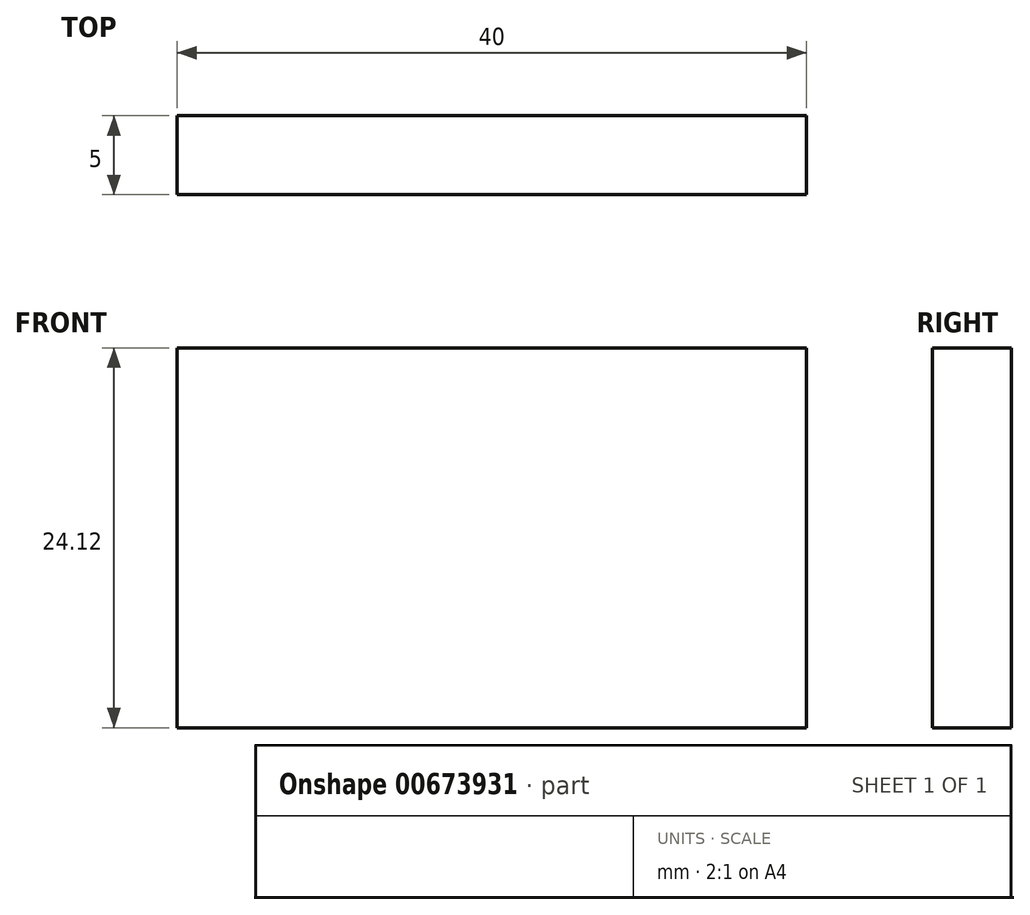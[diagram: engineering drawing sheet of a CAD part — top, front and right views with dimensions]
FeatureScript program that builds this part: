
annotation { "Feature Type Name" : "Feature", "Feature Type Description" : "" }
export const myFeature = defineFeature(function(context is Context, id is Id, definition is map)
    precondition{}
    {
        {
            var Q0;
            Q0=qCreatedBy(makeId("Front.planeOp"),FACE);
            var sketch = newSketch(context, id + "F0", { "sketchPlane" : qUnion([Q0])});
            skLineSegment(sketch, "E0.bottom", {"start": v(49.69, -56.82) * mm, "end": v(7.69, -56.82) * mm});
            skLineSegment(sketch, "E0.top", {"start": v(49.69, 23.18) * mm, "end": v(7.69, 23.18) * mm});
            skLineSegment(sketch, "E0.left", {"start": v(53.69, -52.82) * mm, "end": v(53.69, 19.18) * mm});
            skLineSegment(sketch, "E0.right", {"start": v(3.69, -52.82) * mm, "end": v(3.69, 19.18) * mm});
            skPoint(sketch, "E1.visualSharp", {"position": v(3.69, -56.82) * mm});
            skArc(sketch, "E1.filletArc", {"start": v(3.69, -52.82) * mm, "mid": v(4.86, -55.65) * mm, "end": v(7.69, -56.82) * mm});
            skPoint(sketch, "E2.visualSharp", {"position": v(53.69, -56.82) * mm});
            skArc(sketch, "E2.filletArc", {"start": v(49.69, -56.82) * mm, "mid": v(52.52, -55.65) * mm, "end": v(53.69, -52.82) * mm});
            skPoint(sketch, "E3.visualSharp", {"position": v(53.69, 23.18) * mm});
            skArc(sketch, "E3.filletArc", {"start": v(53.69, 19.18) * mm, "mid": v(52.52, 22) * mm, "end": v(49.69, 23.18) * mm});
            skPoint(sketch, "E4.visualSharp", {"position": v(3.69, 23.18) * mm});
            skArc(sketch, "E4.filletArc", {"start": v(7.69, 23.18) * mm, "mid": v(4.86, 22) * mm, "end": v(3.69, 19.18) * mm});
            skLineSegment(sketch, "E5", {"start": v(3.69, -39.14) * mm, "end": v(53.69, -39.14) * mm});
            skLineSegment(sketch, "E6", {"start": v(48.69, -39.14) * mm, "end": v(48.69, -15.02) * mm});
            skLineSegment(sketch, "E7", {"start": v(48.69, -15.02) * mm, "end": v(8.69, -15.02) * mm});
            skLineSegment(sketch, "E8", {"start": v(8.69, -15.02) * mm, "end": v(8.69, -39.14) * mm});
            skLineSegment(sketch, "E9", {"start": v(8.69, -15.02) * mm, "end": v(3.69, -10.98) * mm});
            skLineSegment(sketch, "E10", {"start": v(3.69, -10.98) * mm, "end": v(3.69, -16.02) * mm});
            skLineSegment(sketch, "E11", {"start": v(3.69, -16.02) * mm, "end": v(8.69, -20.02) * mm});
            skLineSegment(sketch, "E12", {"start": v(48.69, -15.02) * mm, "end": v(53.69, -10.98) * mm});
            skLineSegment(sketch, "E13", {"start": v(48.69, -15.02) * mm, "end": v(48.69, -20.02) * mm});
            skLineSegment(sketch, "E14", {"start": v(48.69, -20.02) * mm, "end": v(53.69, -16.02) * mm});
            skSolve(sketch);
        }
        {
            var Q0;
            {var subQ3=sQuery(id+"F0.wireOp",EDGE,"E6");Q0=makeQuery(id+"F0.imprint","IMPRINT",FACE,{"disambiguationData":[TD([[makeQuery(id+"F0.imprint","IMPRINT",EDGE,{"derivedFrom":subQ3}),1.0]])]});}
            extrude(context, id + "F1", {"entities" : qUnion([Q0]), "depth" : 5 * mm, "offsetDistance" : 25 * mm});
        }
    });
